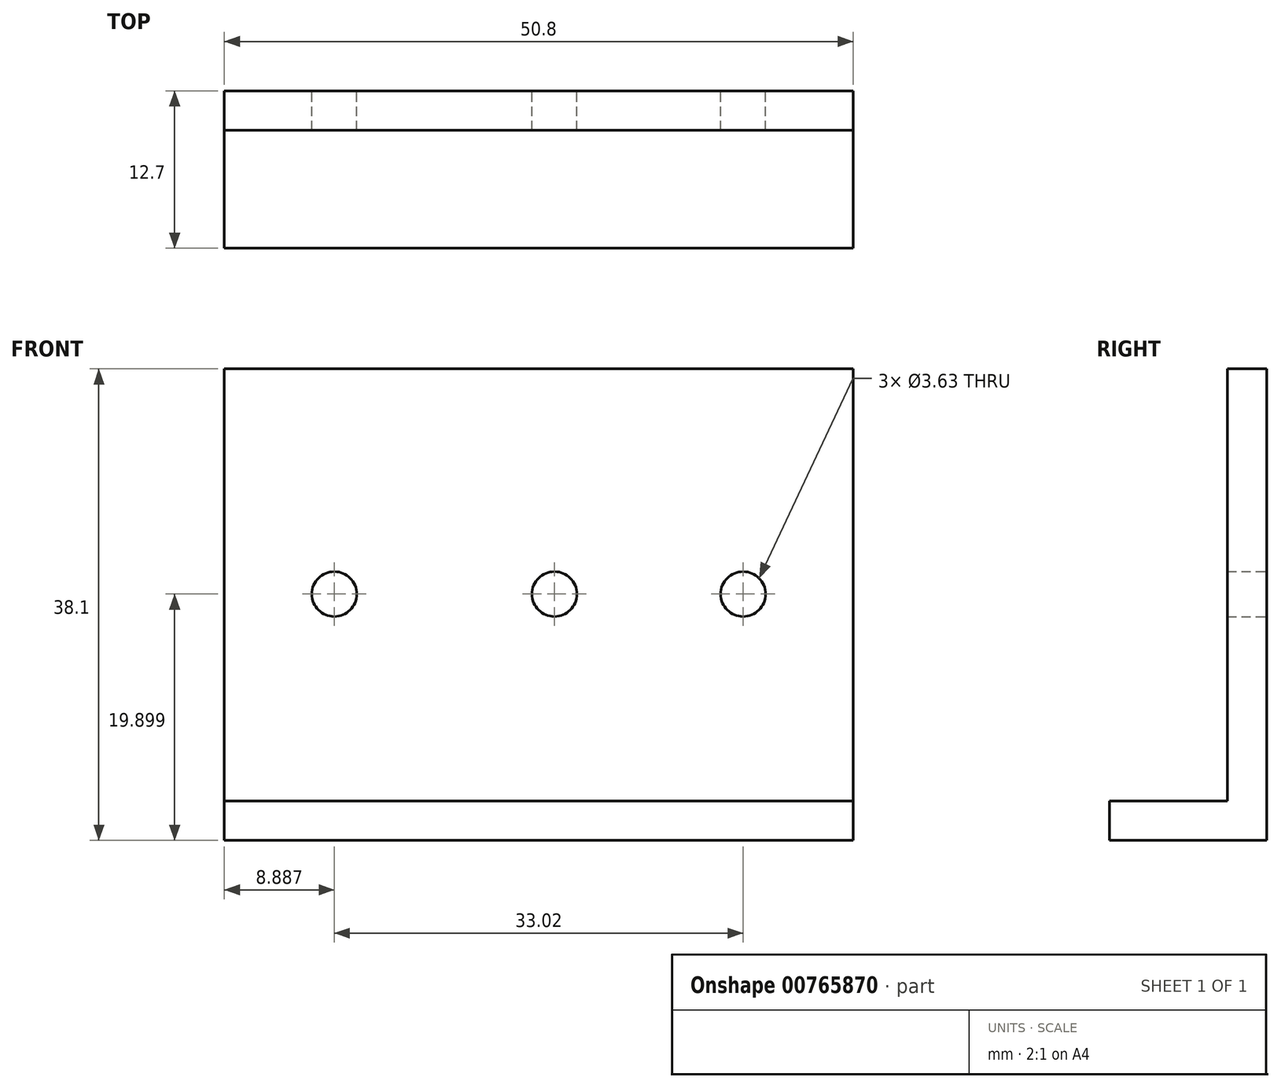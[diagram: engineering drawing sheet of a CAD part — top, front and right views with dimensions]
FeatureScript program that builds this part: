
annotation { "Feature Type Name" : "Feature", "Feature Type Description" : "" }
export const myFeature = defineFeature(function(context is Context, id is Id, definition is map)
    precondition{}
    {
        {
            var Q0;
            Q0=qCreatedBy(makeId("Front.planeOp"),FACE);
            var sketch = newSketch(context, id + "F0", { "sketchPlane" : qUnion([Q0])});
            skLineSegment(sketch, "E0.bottom", {"start": v(-58.45, 45.86) * mm, "end": v(-7.65, 45.86) * mm});
            skLineSegment(sketch, "E0.top", {"start": v(-58.45, 7.76) * mm, "end": v(-7.65, 7.76) * mm});
            skLineSegment(sketch, "E1", {"start": v(-58.45, 10.94) * mm, "end": v(-7.65, 10.94) * mm});
            skCircle(sketch, "E2", {"center": v(-49.56, 27.66) * mm, "radius": 1.81 * mm});
            skCircle(sketch, "E3", {"center": v(-31.78, 27.66) * mm, "radius": 1.81 * mm});
            skCircle(sketch, "E4", {"center": v(-16.54, 27.66) * mm, "radius": 1.81 * mm});
            skLineSegment(sketch, "E5", {"start": v(-7.65, 7.76) * mm, "end": v(-7.65, 45.86) * mm});
            skLineSegment(sketch, "E6", {"start": v(-58.45, 45.86) * mm, "end": v(-58.45, 7.76) * mm});
            skPoint(sketch, "E7.orphan", {"position": v(-65.99, 45.86) * mm});
            skPoint(sketch, "E0.left.end.orphan", {"position": v(-65.99, 7.76) * mm});
            skPoint(sketch, "E0.right.end.orphan", {"position": v(10.21, 7.76) * mm});
            skPoint(sketch, "E0.right.start.orphan", {"position": v(10.21, 10.94) * mm});
            skSolve(sketch);
        }
        {
            var Q0;
            {var subQ2=sQuery(id+"F0.wireOp",EDGE,"E0.bottom");Q0=makeQuery(id+"F0.imprint","IMPRINT",FACE,{"disambiguationData":[TD([[makeQuery(id+"F0.imprint","IMPRINT",EDGE,{"derivedFrom":subQ2}),-1.0]])]});}
            extrude(context, id + "F1", {"entities" : qUnion([Q0]), "depth" : 3.17 * mm, "offsetDistance" : 25.4 * mm});
        }
        {
            var Q0;
            {var subQ1=sQuery(id+"F0.wireOp",EDGE,"E0.top");Q0=makeQuery(id+"F0.imprint","IMPRINT",FACE,{"disambiguationData":[TD([[makeQuery(id+"F0.imprint","IMPRINT",EDGE,{"derivedFrom":subQ1}),1.0]])]});}
            extrude(context, id + "F2", {"entities" : qUnion([Q0]), "operationType" : NewBodyOperationType.ADD, "depth" : 12.7 * mm, "offsetDistance" : 25.4 * mm});
        }
    });
